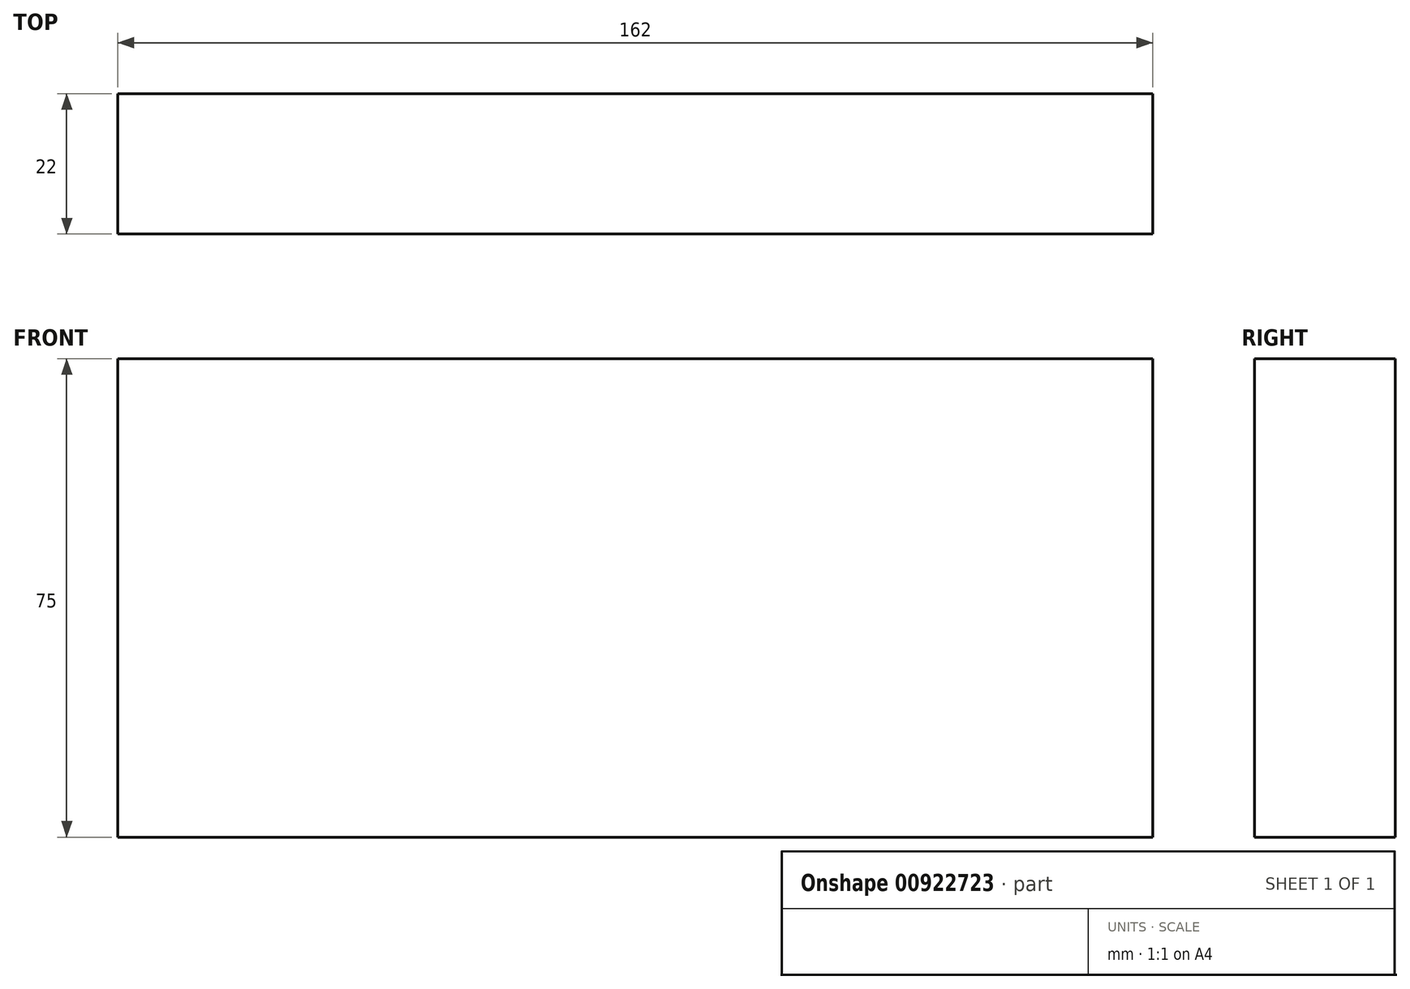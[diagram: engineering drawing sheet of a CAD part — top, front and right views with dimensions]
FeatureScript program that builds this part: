
annotation { "Feature Type Name" : "Feature", "Feature Type Description" : "" }
export const myFeature = defineFeature(function(context is Context, id is Id, definition is map)
    precondition{}
    {
        {
            var Q0;
            Q0=qCreatedBy(makeId("Front.planeOp"),FACE);
            var sketch = newSketch(context, id + "F0", { "sketchPlane" : qUnion([Q0])});
            skLineSegment(sketch, "E0.bottom", {"start": v(-81, -37.5) * mm, "end": v(81, -37.5) * mm});
            skLineSegment(sketch, "E0.top", {"start": v(-81, 37.5) * mm, "end": v(81, 37.5) * mm});
            skLineSegment(sketch, "E0.left", {"start": v(-81, -37.5) * mm, "end": v(-81, 37.5) * mm});
            skLineSegment(sketch, "E0.right", {"start": v(81, -37.5) * mm, "end": v(81, 37.5) * mm});
            skPoint(sketch, "E0.middle", {"position": v(0, 0) * mm});
            skSolve(sketch);
        }
        {
            var Q0;
            Q0 = qSketchRegion(id + "F0", true);
            extrude(context, id + "F1", {"entities" : qUnion([Q0]), "endBound" : BoundingType.SYMMETRIC, "depth" : 22 * mm, "offsetDistance" : 25 * mm});
        }
    });
